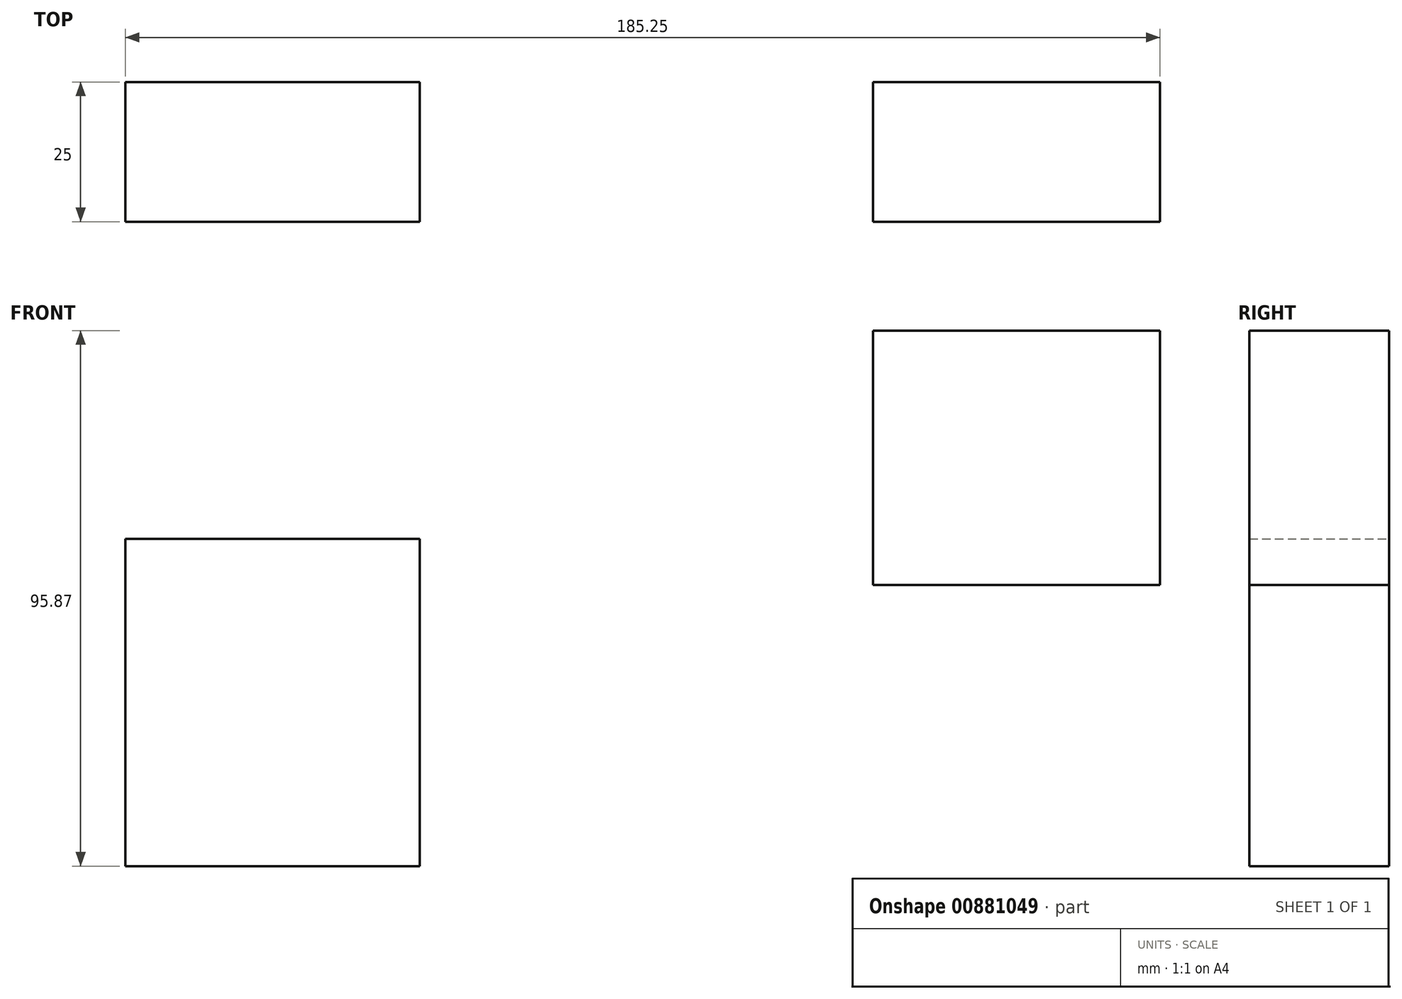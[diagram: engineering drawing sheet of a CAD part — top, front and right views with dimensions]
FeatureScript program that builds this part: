
annotation { "Feature Type Name" : "Feature", "Feature Type Description" : "" }
export const myFeature = defineFeature(function(context is Context, id is Id, definition is map)
    precondition{}
    {
        {
            var Q0;
            Q0=qCreatedBy(makeId("Front.planeOp"),FACE);
            var sketch = newSketch(context, id + "F0", { "sketchPlane" : qUnion([Q0])});
            skLineSegment(sketch, "E0.bottom", {"start": v(-107.31, 7.24) * mm, "end": v(-54.57, 7.24) * mm});
            skLineSegment(sketch, "E0.top", {"start": v(-107.31, 65.86) * mm, "end": v(-54.57, 65.86) * mm});
            skLineSegment(sketch, "E0.left", {"start": v(-107.31, 7.24) * mm, "end": v(-107.31, 65.86) * mm});
            skLineSegment(sketch, "E0.right", {"start": v(-54.57, 7.24) * mm, "end": v(-54.57, 65.86) * mm});
            skPoint(sketch, "E0.middle", {"position": v(-80.94, 36.55) * mm});
            skLineSegment(sketch, "E1.bottom", {"start": v(26.54, 57.56) * mm, "end": v(77.94, 57.56) * mm});
            skLineSegment(sketch, "E1.top", {"start": v(26.54, 103.1) * mm, "end": v(77.94, 103.1) * mm});
            skLineSegment(sketch, "E1.left", {"start": v(26.54, 57.56) * mm, "end": v(26.54, 103.1) * mm});
            skLineSegment(sketch, "E1.right", {"start": v(77.94, 57.56) * mm, "end": v(77.94, 103.1) * mm});
            skPoint(sketch, "E1.middle", {"position": v(52.24, 80.34) * mm});
            skSolve(sketch);
        }
        {
            var Q0;
            Q0=makeQuery(id+"F0.imprint","IMPRINT",FACE,{"disambiguationData":[TD([[makeQuery(id+"F0.imprint","IMPRINT",EDGE,{"derivedFrom":sQuery(id+"F0.wireOp",EDGE,"E0.bottom")}),1.0]])]});
            var Q1;
            Q1=makeQuery(id+"F0.imprint","IMPRINT",FACE,{"disambiguationData":[TD([[makeQuery(id+"F0.imprint","IMPRINT",EDGE,{"derivedFrom":sQuery(id+"F0.wireOp",EDGE,"E1.bottom")}),1.0]])]});
            extrude(context, id + "F1", {"entities" : qUnion([Q0, Q1]), "depth" : 25 * mm, "offsetDistance" : 25 * mm});
        }
    });
